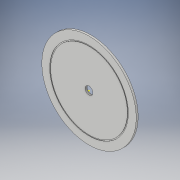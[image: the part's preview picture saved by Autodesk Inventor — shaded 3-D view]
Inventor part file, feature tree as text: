
AUTODESK INVENTOR PART (.ipt)
format: ipt  version: 2019 (Build 230136000, 136)  size: 141,824 bytes
history: native  units: in
note: dims shown in document units (in); Inventor stores cm internally (conversion verified against a paired STEP export)
features: sketch x5, extrude x4
ambient origin geometry x8: Origin, YZ Plane, XZ Plane, XY Plane, X Axis, Y Axis, Z Axis, Center Point
bodies: Solid1 (feature_tree)
feature tree (9):
  extrude  "Extrusion1"  Depth=1.0in
  sketch  "Sketch2"  dims[d2=0.25in d3=0.0in d4=10.0in]
  extrude  "Extrusion2"  Depth=0.25in
  extrude  "Extrusion3"  Depth=0.05in TaperAngle=0.0deg
  extrude  "Extrusion4"  Depth=9.75in
  sketch  "Sketch1"  dims[d0=12.0in d1=1.0in]
  sketch  "Sketch3"  dims[d5=9.75in d6=0.05in d7=0.0in]
  sketch  "Sketch4"  dims[d8=10.0in d9=9.75in]
  sketch  "Sketch5"  dims[d10=0.05in d11=0.0in d12=0.02in d15=0.05in d16=0.05in d17=0.05in d18=0.0in]
